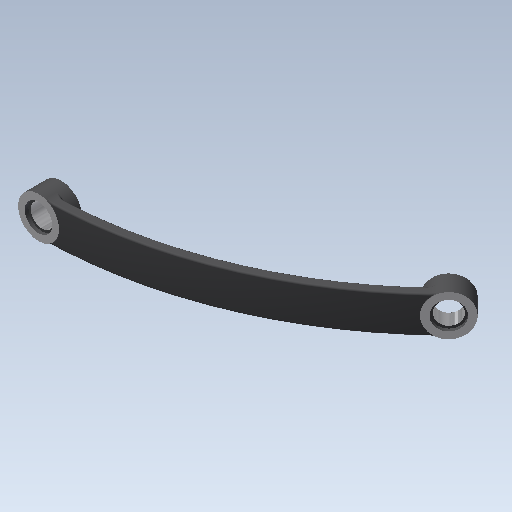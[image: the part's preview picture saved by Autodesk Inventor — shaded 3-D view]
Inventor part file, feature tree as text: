
AUTODESK INVENTOR PART (.ipt)
format: ipt  version: 2020.1 (Build 241239000, 239)  size: 292,864 bytes
history: native  units: mm
features: hole x6, sketch x5, plane x3, extrude x3, fillet x3, other x2, thicken_offset x1, revolve x1
ambient origin geometry x8: Origin, YZ Plane, XZ Plane, XY Plane, X Axis, Y Axis, Z Axis, Center Point
bodies: Solid1 (feature_tree)
feature tree (24):
  sketch  "3D Sketch1"
  plane  "Work Plane1"
  sketch  "Sketch2"  dims[d2=180.0mm d4=180.0mm]
  thicken_offset  "Thicken1"
  extrude  "Extrusion1"  TaperAngle=180.0deg  [1 undecoded]
  plane  "Work Plane2"
  extrude  "Extrusion2"  Depth=180.0mm
  plane  "Work Plane3"
  extrude  "Extrusion3"  Depth=4.0mm
  hole  "Hole1"  [1 undecoded]
  hole  "Hole2"  [1 undecoded]
  fillet  "Fillet1"  Radius=18.0mm
  fillet  "Fillet2"  Radius=10.0mm
  fillet  "Fillet3"  Radius=10.0mm
  hole  "Hole4"  [1 undecoded]
  hole  "Hole5"  [1 undecoded]
  hole  "Hole6"  [1 undecoded]
  hole  "Hole7"  [1 undecoded]
  sketch  "Sketch1"  dims[d0=180.0mm d1=180.0deg]
  other  "Srf1"
  sketch  "Sketch3"  dims[d5=16.0mm d6=4.0mm d7=8.0mm]
  sketch  "Sketch4"  dims[d8=10.0mm d9=0.0mm d10=18.0mm d11=10.0mm d12=0.0mm d13=18.0mm d14=10.0mm d15=0.0mm d16=10.0mm d17=10.0mm d18=10.0mm d19=6.0mm d20=4.0mm d21=2.0mm d22=90.0deg d23=8.0mm d24=20.594885mm d25=10.0mm d26=10.0mm d27=10.0mm d28=6.0mm d29=4.0mm d30=2.0mm d31=90.0deg d32=8.0mm d33=20.594885mm d34=1.0mm d35=10.0mm d36=0.7mm d52=45.0deg d53=10.0mm d54=10.0mm d55=12.0mm d56=6.0mm d57=4.0mm d58=2.0mm d59=90.0deg d60=1.5mm d61=0.0mm d62=10.0mm d63=10.0mm d64=12.0mm d65=6.0mm d66=4.0mm d67=2.0mm d68=90.0deg d69=1.5mm d70=0.0mm d71=10.0mm d72=10.0mm d73=12.0mm d74=6.0mm d75=4.0mm d76=2.0mm d77=90.0deg d78=1.5mm d79=0.0mm d80=10.0mm d81=10.0mm d82=12.0mm d83=6.0mm d84=4.0mm d85=2.0mm d86=90.0deg d87=1.5mm d88=0.0mm]
  revolve  "RevolutionSrf1"  Angle=45.0deg
  other  "3D Intersection1"
note: 7 required parameter values undecoded (feature->parameter linkage not recoverable at this tier; creation-order binding heuristic only, values carry confidence <= 0.55)
